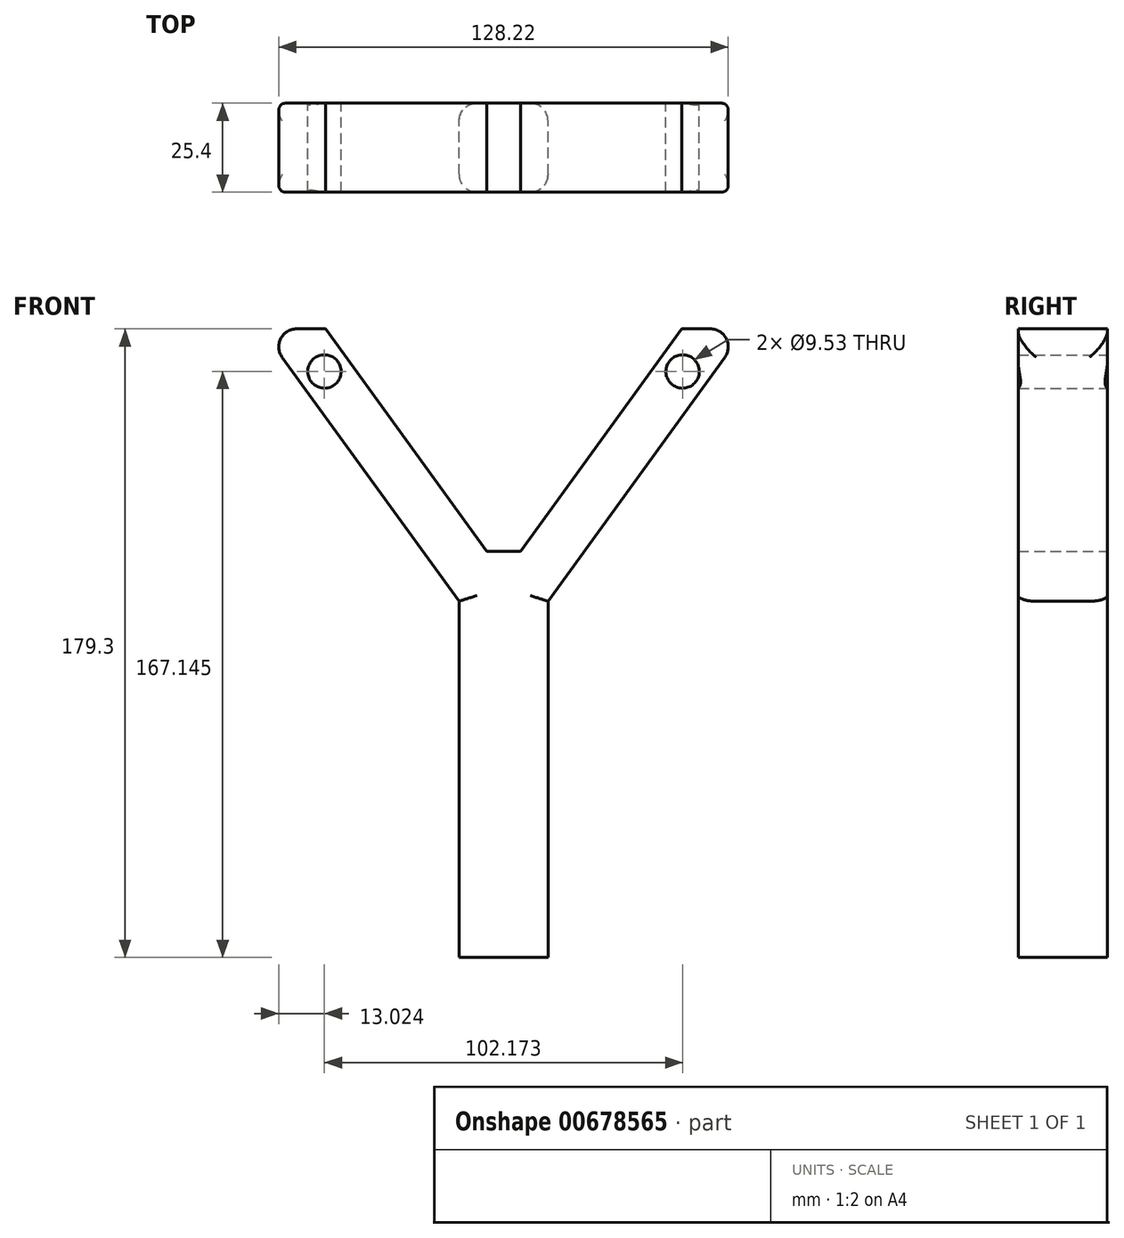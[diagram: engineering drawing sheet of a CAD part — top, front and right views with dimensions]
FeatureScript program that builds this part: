
annotation { "Feature Type Name" : "Feature", "Feature Type Description" : "" }
export const myFeature = defineFeature(function(context is Context, id is Id, definition is map)
    precondition{}
    {
        {
            var Q0;
            Q0=qCreatedBy(makeId("Front.planeOp"),FACE);
            var sketch = newSketch(context, id + "F0", { "sketchPlane" : qUnion([Q0])});
            skLineSegment(sketch, "E0", {"start": v(0, 0) * mm, "end": v(4.8, 0) * mm});
            skLineSegment(sketch, "E1", {"start": v(4.8, 0) * mm, "end": v(50.8, 63.5) * mm});
            skLineSegment(sketch, "E2", {"start": v(50.8, 63.5) * mm, "end": v(68.98, 63.5) * mm});
            skLineSegment(sketch, "E3", {"start": v(68.98, 63.5) * mm, "end": v(12.7, -14.2) * mm});
            skLineSegment(sketch, "E4", {"start": v(12.7, -14.2) * mm, "end": v(12.7, -115.8) * mm});
            skLineSegment(sketch, "E5", {"start": v(12.7, -115.8) * mm, "end": v(0, -115.8) * mm});
            skLineSegment(sketch, "E6", {"start": v(0, 0) * mm, "end": v(0, -115.8) * mm, "construction": true});
            skLineSegment(sketch, "E7.MirrorCS", {"start": v(-12.7, -14.2) * mm, "end": v(-12.7, -115.8) * mm});
            skLineSegment(sketch, "E8.MirrorCS", {"start": v(-68.98, 63.5) * mm, "end": v(-12.7, -14.2) * mm});
            skLineSegment(sketch, "E9.MirrorCS", {"start": v(-50.8, 63.5) * mm, "end": v(-68.98, 63.5) * mm});
            skLineSegment(sketch, "E10.MirrorCS", {"start": v(0, 0) * mm, "end": v(-4.8, 0) * mm});
            skLineSegment(sketch, "E11.MirrorCS", {"start": v(-4.8, 0) * mm, "end": v(-50.8, 63.5) * mm});
            skLineSegment(sketch, "E12.MirrorCS", {"start": v(-12.7, -115.8) * mm, "end": v(0, -115.8) * mm});
            skSolve(sketch);
        }
        {
            var Q0;
            Q0 = qSketchRegion(id + "F0", true);
            extrude(context, id + "F1", {"entities" : qUnion([Q0]), "depth" : 25.4 * mm, "offsetDistance" : 25.4 * mm});
        }
        {
            var Q0;
            Q0=makeQuery(id+"F1.opExtrude","CAP_FACE",FACE,{"disambiguationData":[OSD([sQuery(id+"F0.wireOp",EDGE,"E0"),sQuery(id+"F0.wireOp",EDGE,"E1"),sQuery(id+"F0.wireOp",EDGE,"E2"),sQuery(id+"F0.wireOp",EDGE,"E3"),sQuery(id+"F0.wireOp",EDGE,"E4"),sQuery(id+"F0.wireOp",EDGE,"E5"),sQuery(id+"F0.wireOp",EDGE,"E7.MirrorCS"),sQuery(id+"F0.wireOp",EDGE,"E8.MirrorCS"),sQuery(id+"F0.wireOp",EDGE,"E9.MirrorCS"),sQuery(id+"F0.wireOp",EDGE,"E10.MirrorCS"),sQuery(id+"F0.wireOp",EDGE,"E11.MirrorCS"),sQuery(id+"F0.wireOp",EDGE,"E12.MirrorCS")])],"isStart":true});
            var sketch = newSketch(context, id + "F2", { "sketchPlane" : qUnion([Q0])});
            skLineSegment(sketch, "E13", {"start": v(-60.18, 51.35) * mm, "end": v(-42, 51.35) * mm});
            skLineSegment(sketch, "E14", {"start": v(42, 51.35) * mm, "end": v(60.18, 51.35) * mm});
            skCircle(sketch, "E15", {"center": v(-51.09, 51.35) * mm, "radius": 4.76 * mm});
            skCircle(sketch, "E16", {"center": v(51.09, 51.35) * mm, "radius": 4.76 * mm});
            skSolve(sketch);
        }
        {
            var Q0;
            Q0 = qSketchRegion(id + "F2", true);
            extrude(context, id + "F3", {"entities" : qUnion([Q0]), "operationType" : NewBodyOperationType.REMOVE, "endBound" : BoundingType.THROUGH_ALL, "oppositeDirection" : true, "depth" : 25.4 * mm, "offsetDistance" : 25.4 * mm});
        }
        {
            var Q0;
            Q0=makeQuery(id+"F1.opExtrude","CAP_EDGE",EDGE,{"disambiguationData":[OSD([sQuery(id+"F0.wireOp",EDGE,"E4")])],"isStart":true});
            var Q1;
            Q1=makeQuery(id+"F1.opExtrude","CAP_EDGE",EDGE,{"disambiguationData":[OSD([sQuery(id+"F0.wireOp",EDGE,"E7.MirrorCS")])],"isStart":true});
            var Q2;
            Q2=makeQuery(id+"F1.opExtrude","CAP_EDGE",EDGE,{"disambiguationData":[OSD([sQuery(id+"F0.wireOp",EDGE,"E4")])],"isStart":false});
            var Q3;
            Q3=makeQuery(id+"F1.opExtrude","CAP_EDGE",EDGE,{"disambiguationData":[OSD([sQuery(id+"F0.wireOp",EDGE,"E7.MirrorCS")])],"isStart":false});
            var Q4;
            Q4=makeQuery(id+"F1.opExtrude","CAP_EDGE",EDGE,{"disambiguationData":[OSD([sQuery(id+"F0.wireOp",EDGE,"E3")])],"isStart":false});
            var Q5;
            Q5=makeQuery(id+"F1.opExtrude","CAP_EDGE",EDGE,{"disambiguationData":[OSD([sQuery(id+"F0.wireOp",EDGE,"E3")])],"isStart":true});
            var Q6;
            Q6=makeQuery(id+"F1.opExtrude","CAP_EDGE",EDGE,{"disambiguationData":[OSD([sQuery(id+"F0.wireOp",EDGE,"E8.MirrorCS")])],"isStart":false});
            var Q7;
            Q7=makeQuery(id+"F1.opExtrude","CAP_EDGE",EDGE,{"disambiguationData":[OSD([sQuery(id+"F0.wireOp",EDGE,"E8.MirrorCS")])],"isStart":true});
            var Q8;
            Q8=makeQuery(id+"F1.opExtrude","SWEPT_EDGE",EDGE,{"disambiguationData":[OSD([sQuery(id+"F0.wireOp",EDGE,"E8.MirrorCS"),sQuery(id+"F0.wireOp",EDGE,"E9.MirrorCS")])]});
            var Q9;
            Q9=makeQuery(id+"F1.opExtrude","SWEPT_EDGE",EDGE,{"disambiguationData":[OSD([sQuery(id+"F0.wireOp",EDGE,"E2"),sQuery(id+"F0.wireOp",EDGE,"E3")])]});
            fillet(context, id + "F4", {"entities" : qUnion([Q0, Q1, Q2, Q3, Q4, Q5, Q6, Q7, Q8, Q9]), "radius" : 5.08 * mm, "tangentPropagation" : true, "allowEdgeOverflow" : false});
        }
    });
